# Revit family: ASSA_ABLOY_VersaMax_Touchless_OHC_FSL01
name_source: partatom
category: Doors
units: mm (PartAtom-declared; Revit-internal decimal feet)

## family parameters
Always vertical = Yes
Cut with Voids When Loaded = No
Host = Wall
OmniClass Number = 23.30.10.00
OmniClass Title = Doors
Room Calculation Point = No
Shared = No

## types (4) — shared parameters
Analytic Construction = <None>
BIMobject category = Sliding Doors
Bottom Profile Height = Fix Leaf : 0'4''
Bottom Profile Option 01 = Fix Leaf : 0'4''
Bottom Profile Option 02 = Fix Leaf : 0'7''
Bottom Profile Option 03 = Fix Leaf : 0'10''
Brass Polished Finish = Brass, Polished
Brass Satin Finish = Brass, Satin
Clear Anodized = Clear Anodized
Dark Bronze Anodized = Dark Bronze Anodized
Date of publishing = 2015-02-23
Depth = 0.00
Edition number = 1
Frame Material = Clear Anodized
Gap = 0' - 0 1/4"
Glass = Glass
Height = 7' - 5 3/4"
IFC Classification = Door
Leaf Height = 7' - 1"
Manufacturer = ASSA ABLOY Entrance Systems-North America
Manufacturer name = ASSA ABLOY Entrance Systems-North America
Material main = Aluminium
NBS Reference Code = 25-30-20-77
NBS Reference Description = Sliding Doorset Systems
Nominal height = 0.00
Nominal width = 0.00
Product SKU = VersaMax_Touchless_OHC
Product data url = http://besam-na.bimobject.com
Product family = ICU
Product group = Touchless
QR code = http://besam-na.bimobject.com
Rough Height = 7' - 6"
Stainless Steel Polished Finish = Stainless Steel, Polished
Stainless Steel Satin Finish = Stainless Steel, Satin
Thickness = 0' - 0"
UNSPSC Code = 301715
Uniclass 1.4 Code = L4133
Uniclass 1.4 Description = Sliding
Uniclass 2.0 Code = SS-25-30-20-77
Uniclass 2.0 Description = Sliding Doorset Systems
Wall Closure = By host
Weight Net (Kg) = 0

## per-type parameters (varying)
| type | Leaf Width | Rough Width | Top Profile Height | Width |
| ICU-SE-2FBO-7 | 3' - 5 1/2" | 7' - 0 1/2" | 0' - 4" | 7' - 0" |
| ICU-SE-2FBO-8 | 3' - 11 1/2" | 8' - 0 1/2" | 0' - 7" | 8' - 0" |
| ICU-SE-2FBO-8-6 | 4' - 2 1/2" | 8' - 6 1/2" | 0' - 7" | 8' - 6" |
| ICU-SE-2FBO-9 | 4' - 5 1/2" | 9' - 0 1/2" | 0' - 4" | 9' - 0" |

## geometry (parser evidence)
native form markers: Blend x2, Sweep x20
no freeform markers — native parametric forms only
